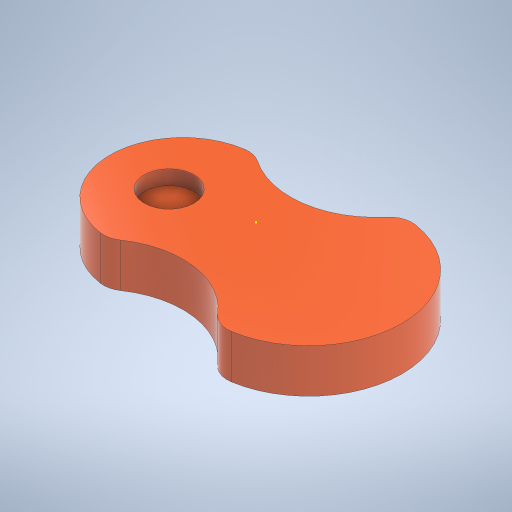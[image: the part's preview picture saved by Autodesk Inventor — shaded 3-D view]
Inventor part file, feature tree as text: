
AUTODESK INVENTOR PART (.ipt)
format: ipt  version: 2024 (Build 280153020, 153B)  size: 286,208 bytes
history: native  units: mm
features: sketch x6, extrude x5, fillet x4
ambient origin geometry x8: Origin, YZ Plane, XZ Plane, XY Plane, X Axis, Y Axis, Z Axis, Center Point
bodies: Solid1 (feature_tree)
feature tree (15):
  extrude  "Extrusion1"  Depth=10.0mm TaperAngle=0.0deg
  extrude  "Extrusion2"  Depth=2.5mm TaperAngle=0.0deg
  sketch  "Sketch8"  dims[d17=32.0mm d18=15.0mm d19=0.0mm d20=4.0mm d21=4.0mm d22=4.0mm d23=4.0mm]
  extrude  "Extrusion6"  Depth=4.0mm TaperAngle=0.0deg
  fillet  "Fillet3"  Radius=4.0mm
  fillet  "Fillet4"  Radius=4.0mm
  fillet  "Fillet5"  Radius=4.0mm
  fillet  "Fillet6"  Radius=4.0mm
  extrude  "Extrusion7"  Depth=2.5mm
  extrude  "Extrusion8"  Depth=2.5mm
  sketch  "Sketch1"  dims[d0=50.0mm d1=10.0mm d2=0.0mm]
  sketch  "Sketch2"  dims[d3=8.3mm d4=2.5mm d5=0.0mm]
  sketch  "Sketch9"  dims[d24=2.5mm d25=0.0mm d26=8.5mm]
  sketch  "Sketch10"  dims[d27=2.5mm d28=0.0mm d32=0.5mm]
  sketch  "Sketch11"  dims[d33=0.872665mm d34=0.5mm d35=0.872665mm]
